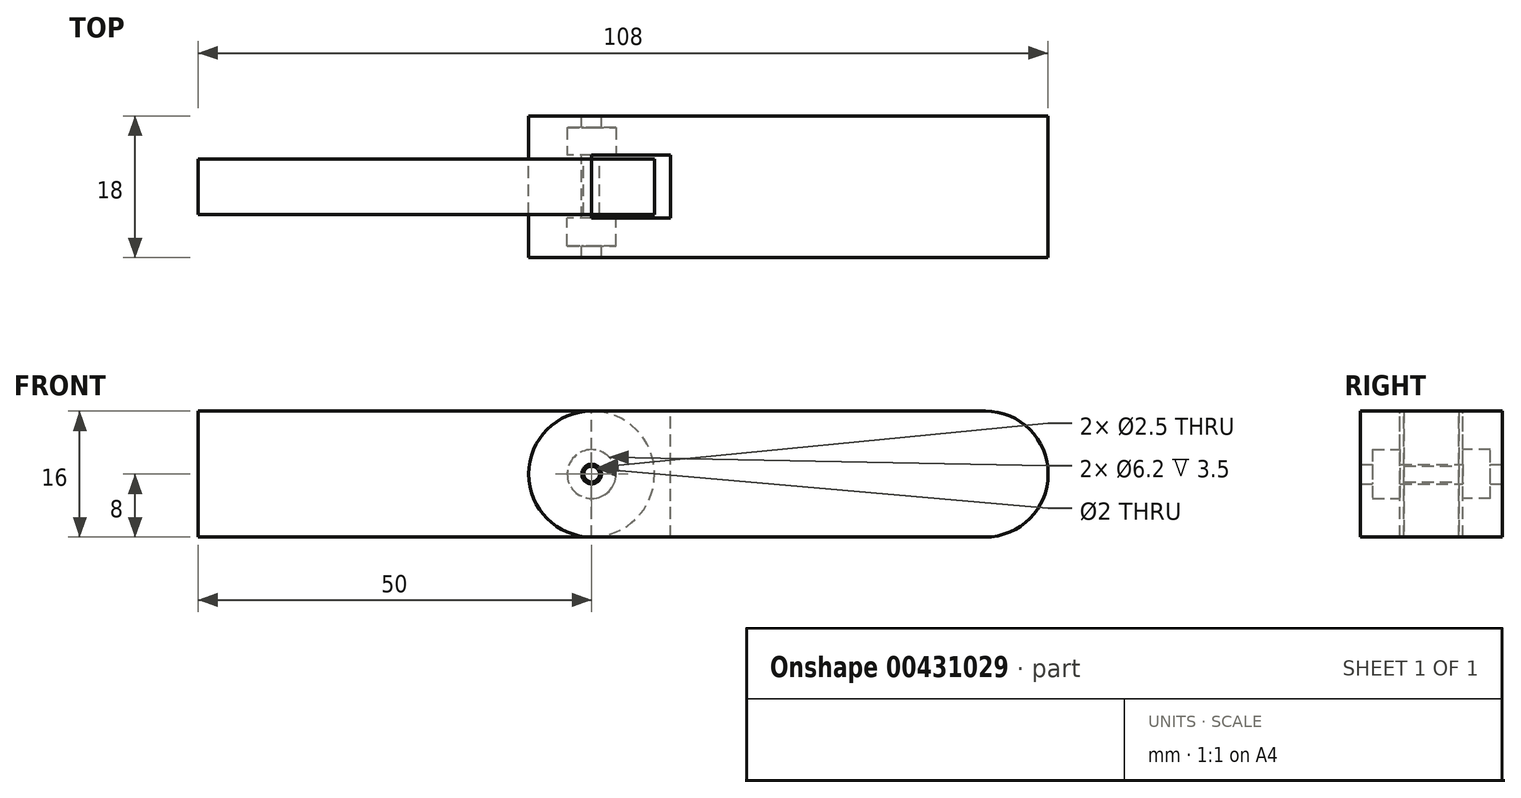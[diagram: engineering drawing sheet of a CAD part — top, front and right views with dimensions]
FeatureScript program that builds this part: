
annotation { "Feature Type Name" : "Feature", "Feature Type Description" : "" }
export const myFeature = defineFeature(function(context is Context, id is Id, definition is map)
    precondition{}
    {
        {
            var Q0;
            Q0=qCreatedBy(makeId("Front.planeOp"),FACE);
            var sketch = newSketch(context, id + "F0", { "sketchPlane" : qUnion([Q0])});
            skCircle(sketch, "E0", {"center": v(0, 0) * mm, "radius": 1.25 * mm});
            skArc(sketch, "E1", {"start": v(0, 8) * mm, "mid": v(-8, 0) * mm, "end": v(0, -8) * mm});
            skLineSegment(sketch, "E2", {"start": v(0, 8) * mm, "end": v(50, 8) * mm});
            skLineSegment(sketch, "E3", {"start": v(0, -8) * mm, "end": v(50, -8) * mm});
            skArc(sketch, "E4", {"start": v(50, 8) * mm, "mid": v(58, 0) * mm, "end": v(50, -8) * mm});
            skSolve(sketch);
        }
        {
            var Q0;
            Q0=makeQuery(id+"F0.imprint","IMPRINT",FACE,{"disambiguationData":[TD([[makeQuery(id+"F0.imprint","IMPRINT",EDGE,{"derivedFrom":sQuery(id+"F0.wireOp",EDGE,"E0")}),-1.0]])]});
            extrude(context, id + "F1", {"entities" : qUnion([Q0]), "depth" : 9 * mm, "hasSecondDirection" : true, "secondDirectionOppositeDirection" : true, "secondDirectionDepth" : 9 * mm});
        }
        {
            var Q0;
            Q0=makeQuery(id+"F1.opExtrude","SWEPT_FACE",FACE,{"disambiguationData":[OSD([sQuery(id+"F0.wireOp",EDGE,"E2")])]});
            var sketch = newSketch(context, id + "F2", { "sketchPlane" : qUnion([Q0])});
            skLineSegment(sketch, "E5", {"start": v(-8, -5) * mm, "end": v(-8, 5) * mm});
            skLineSegment(sketch, "E6.0", {"start": v(0, 9) * mm, "end": v(50, 9) * mm});
            skLineSegment(sketch, "E7.0", {"start": v(0, -9) * mm, "end": v(50, -9) * mm});
            skLineSegment(sketch, "E8.0", {"start": v(0, -9) * mm, "end": v(0, 9) * mm});
            skLineSegment(sketch, "E9", {"start": v(-8, 0) * mm, "end": v(-8, 4) * mm});
            skLineSegment(sketch, "E10", {"start": v(-8, 4) * mm, "end": v(0, 4) * mm});
            skLineSegment(sketch, "E11", {"start": v(0, 4) * mm, "end": v(10, 4) * mm});
            skLineSegment(sketch, "E12", {"start": v(10, 4) * mm, "end": v(10, 0) * mm});
            skLineSegment(sketch, "E13", {"start": v(10, 0) * mm, "end": v(10, -4) * mm});
            skLineSegment(sketch, "E14", {"start": v(10, -4) * mm, "end": v(0, -4) * mm});
            skLineSegment(sketch, "E15", {"start": v(0, -4) * mm, "end": v(-8, -4) * mm});
            skLineSegment(sketch, "E16", {"start": v(-8, -4) * mm, "end": v(-8, 0) * mm});
            skSolve(sketch);
        }
        {
            var Q0;
            Q0=makeQuery(id+"F2.imprint","IMPRINT",FACE,{"disambiguationData":[TD([[makeQuery(id+"F2.imprint","IMPRINT",EDGE,{"derivedFrom":sQuery(id+"F2.wireOp",EDGE,"E9")}),-1.0]])]});
            var Q1;
            {var subQ0=sQuery(id+"F2.wireOp",EDGE,"E11");Q1=makeQuery(id+"F2.imprint","IMPRINT",FACE,{"disambiguationData":[TD([[makeQuery(id+"F2.imprint","IMPRINT",EDGE,{"derivedFrom":subQ0}),-1.0]])]});}
            var Q2;
            Q2=makeQuery(id+"F1.opExtrude","SWEPT_FACE",FACE,{"disambiguationData":[OSD([sQuery(id+"F0.wireOp",EDGE,"E3")])]});
            extrude(context, id + "F3", {"entities" : qUnion([Q0, Q1]), "operationType" : NewBodyOperationType.REMOVE, "endBound" : BoundingType.UP_TO_SURFACE, "oppositeDirection" : true, "endBoundEntityFace" : qUnion([Q2]), "depth" : 25 * mm});
        }
        {
            var Q0;
            Q0=makeQuery(id+"F3.boolean.opBoolean","COPY",FACE,{"derivedFrom":makeQuery(id+"F3.opExtrude","SWEPT_FACE",FACE,{"disambiguationData":[OSD([sQuery(id+"F2.wireOp",EDGE,"E10"),sQuery(id+"F2.wireOp",EDGE,"E11")])]})});
            var sketch = newSketch(context, id + "F4", { "sketchPlane" : qUnion([Q0])});
            skCircle(sketch, "E17", {"center": v(0, 0) * mm, "radius": 3.1 * mm});
            skSolve(sketch);
        }
        {
            var Q0;
            Q0=makeQuery(id+"F4.imprint","IMPRINT",FACE,{"disambiguationData":[TD([[makeQuery(id+"F4.imprint","IMPRINT",EDGE,{"derivedFrom":sQuery(id+"F4.wireOp",EDGE,"E17")}),1.0]])]});
            extrude(context, id + "F5", {"entities" : qUnion([Q0]), "operationType" : NewBodyOperationType.REMOVE, "oppositeDirection" : true, "depth" : 3.5 * mm});
        }
        {
            var Q0;
            Q0=makeQuery(id+"F3.boolean.opBoolean","COPY",FACE,{"derivedFrom":makeQuery(id+"F3.opExtrude","SWEPT_FACE",FACE,{"disambiguationData":[OSD([sQuery(id+"F2.wireOp",EDGE,"E14"),sQuery(id+"F2.wireOp",EDGE,"E15")])]})});
            var sketch = newSketch(context, id + "F6", { "sketchPlane" : qUnion([Q0])});
            skCircle(sketch, "E18", {"center": v(0, 0) * mm, "radius": 3.1 * mm});
            skSolve(sketch);
        }
        {
            var Q0;
            Q0=makeQuery(id+"F6.imprint","IMPRINT",FACE,{"disambiguationData":[TD([[makeQuery(id+"F6.imprint","IMPRINT",EDGE,{"derivedFrom":sQuery(id+"F6.wireOp",EDGE,"E18")}),1.0]])]});
            extrude(context, id + "F7", {"entities" : qUnion([Q0]), "operationType" : NewBodyOperationType.REMOVE, "oppositeDirection" : true, "depth" : 3.5 * mm});
        }
        {
            var Q0;
            Q0=qCreatedBy(makeId("Front.planeOp"),FACE);
            var sketch = newSketch(context, id + "F8", { "sketchPlane" : qUnion([Q0])});
            skCircle(sketch, "E19", {"center": v(0, 0) * mm, "radius": 1 * mm});
            skLineSegment(sketch, "E20.0", {"start": v(0, 8) * mm, "end": v(50, 8) * mm});
            skLineSegment(sketch, "E21.0", {"start": v(0, -8) * mm, "end": v(50, -8) * mm});
            skArc(sketch, "E22", {"start": v(0, 8) * mm, "mid": v(8, 0) * mm, "end": v(0, -8) * mm});
            skLineSegment(sketch, "E23", {"start": v(0, 8) * mm, "end": v(-50, 8) * mm});
            skLineSegment(sketch, "E24", {"start": v(-50, 8) * mm, "end": v(-50, -8) * mm});
            skLineSegment(sketch, "E25", {"start": v(-50, -8) * mm, "end": v(0, -8) * mm});
            skSolve(sketch);
        }
        {
            var Q0;
            Q0=makeQuery(id+"F8.imprint","IMPRINT",FACE,{"disambiguationData":[TD([[makeQuery(id+"F8.imprint","IMPRINT",EDGE,{"derivedFrom":sQuery(id+"F8.wireOp",EDGE,"E19")}),-1.0]])]});
            extrude(context, id + "F9", {"entities" : qUnion([Q0]), "depth" : 3.5 * mm, "hasSecondDirection" : true, "secondDirectionOppositeDirection" : true, "secondDirectionDepth" : 3.5 * mm});
        }
    });
